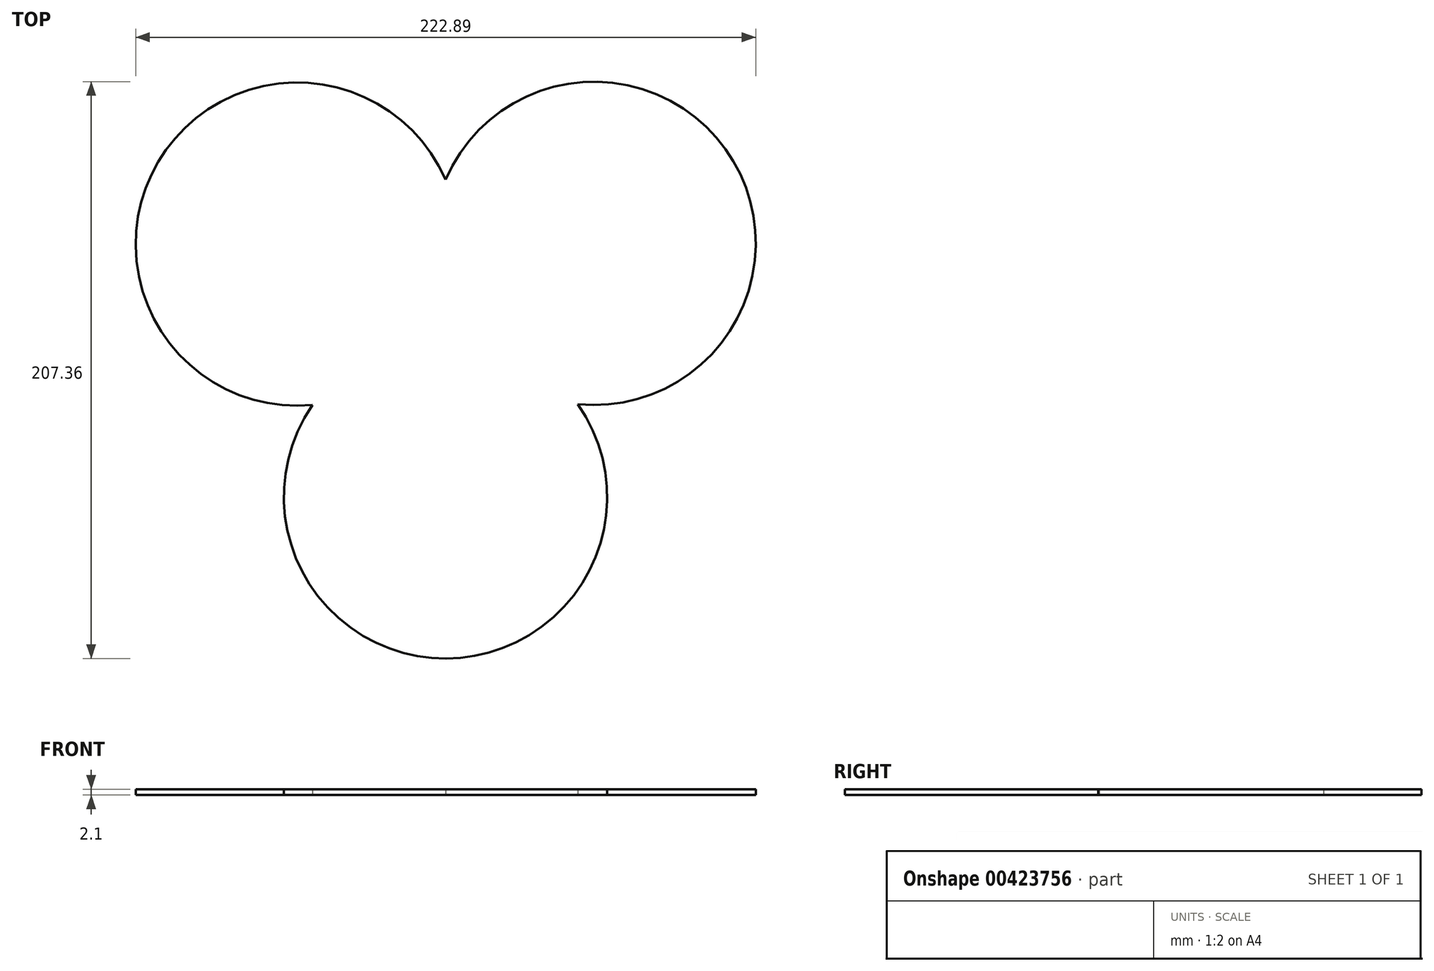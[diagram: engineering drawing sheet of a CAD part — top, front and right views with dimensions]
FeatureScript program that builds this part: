
annotation { "Feature Type Name" : "Feature", "Feature Type Description" : "" }
export const myFeature = defineFeature(function(context is Context, id is Id, definition is map)
    precondition{}
    {
        {
            var Q0;
            Q0=qCreatedBy(makeId("Top.planeOp"),FACE);
            var sketch = newSketch(context, id + "F0", { "sketchPlane" : qUnion([Q0])});
            skPoint(sketch, "E0.0.midPoint", {"position": v(0, 44) * mm});
            skArc(sketch, "E1.0", {"start": v(67.96, -38.95) * mm, "mid": v(147.8, 85.79) * mm, "end": v(0, 76.29) * mm});
            skArc(sketch, "E2.0", {"start": v(-68.29, -39.43) * mm, "mid": v(0.29, -169.6) * mm, "end": v(67.96, -38.95) * mm});
            skArc(sketch, "E2.1", {"start": v(0, 76.29) * mm, "mid": v(-147.6, 85.39) * mm, "end": v(-68.29, -39.43) * mm});
            skPoint(sketch, "E3.center.orphan", {"position": v(-64.95, 44) * mm});
            skPoint(sketch, "E4.center.orphan", {"position": v(64.95, 44) * mm});
            skSolve(sketch);
        }
        {
            var Q0;
            Q0=makeQuery(id+"F0.imprint","IMPRINT",FACE,{"disambiguationData":[TD([[makeQuery(id+"F0.imprint","IMPRINT",EDGE,{"derivedFrom":sQuery(id+"F0.wireOp",EDGE,"E2.0")}),1.0]])]});
            extrude(context, id + "F1", {"entities" : qUnion([Q0]), "depth" : 3 * mm});
        }
        {
            var Q0;
            Q0=makeQuery(id+"F1.opExtrude","SWEPT_BODY",BODY,{"disambiguationData":[OSD([sQuery(id+"F0.wireOp",EDGE,"E2.0"),sQuery(id+"F0.wireOp",EDGE,"E1.0"),sQuery(id+"F0.wireOp",EDGE,"E2.1")])]});
            var Q1;
            Q1=qCreatedBy(makeId("Origin.pointOp"),VERTEX);
            transform(context, id + "F2", {"entities" : qUnion([Q0]), "transformType" : TransformType.SCALE_UNIFORMLY, "scale" : 0.7, "scalePoint" : qUnion([Q1]), "makeCopy" : false});
        }
    });
